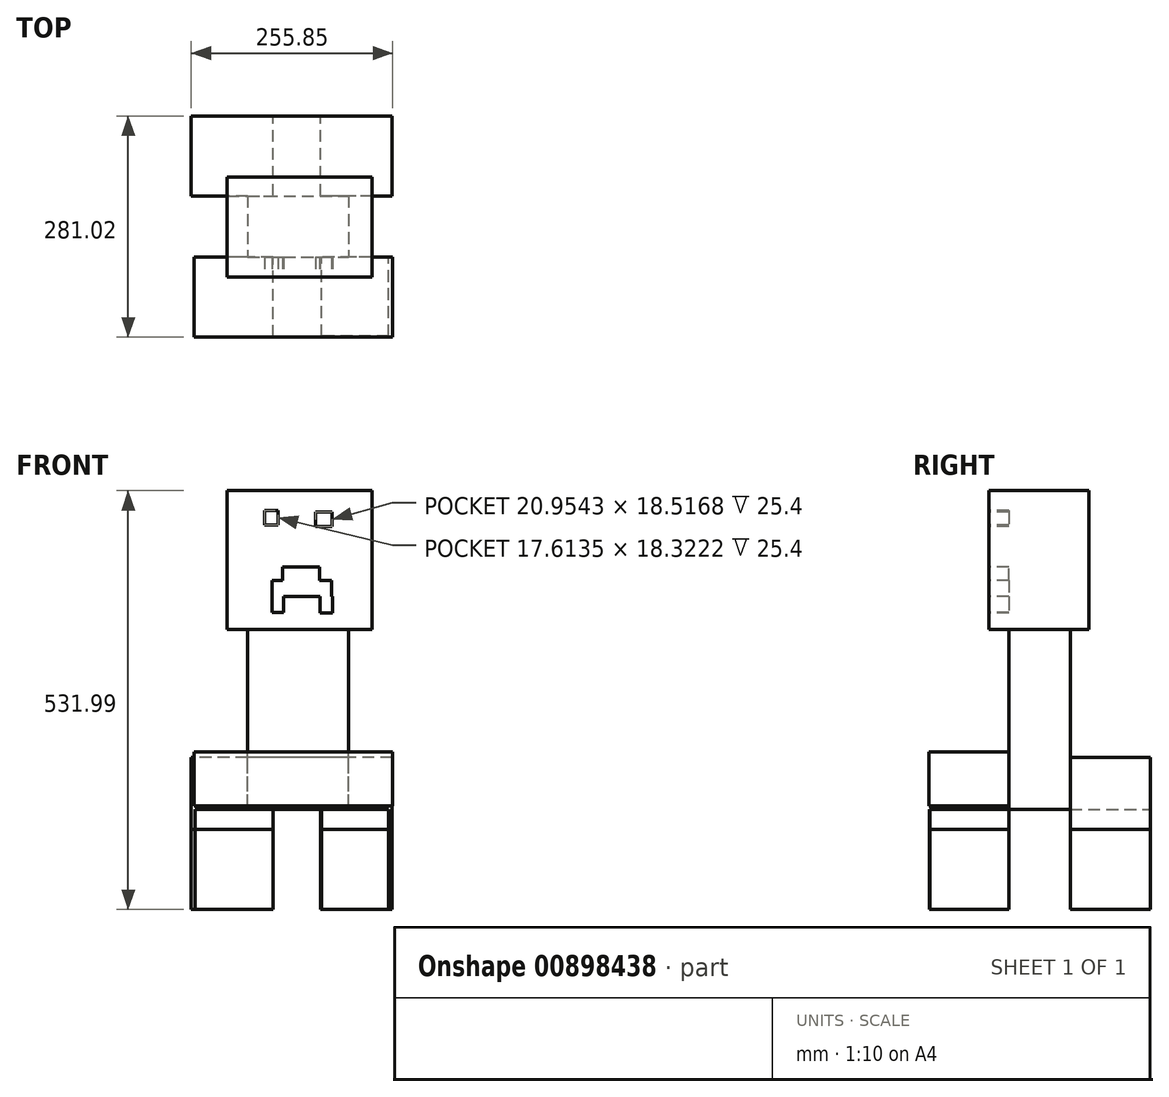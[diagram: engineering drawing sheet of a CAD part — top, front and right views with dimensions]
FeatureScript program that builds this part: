
annotation { "Feature Type Name" : "Feature", "Feature Type Description" : "" }
export const myFeature = defineFeature(function(context is Context, id is Id, definition is map)
    precondition{}
    {
        {
            var Q0;
            Q0=qCreatedBy(makeId("Front.planeOp"),FACE);
            var sketch = newSketch(context, id + "F0", { "sketchPlane" : qUnion([Q0])});
            skLineSegment(sketch, "E0.bottom", {"start": v(0, 0) * mm, "end": v(133.56, 0) * mm});
            skLineSegment(sketch, "E0.top", {"start": v(0, 176.39) * mm, "end": v(133.56, 176.39) * mm});
            skLineSegment(sketch, "E0.left", {"start": v(0, 0) * mm, "end": v(0, 176.39) * mm});
            skLineSegment(sketch, "E0.right", {"start": v(133.56, 0) * mm, "end": v(133.56, 176.39) * mm});
            skSolve(sketch);
        }
        {
            var Q0;
            Q0 = qSketchRegion(id + "F0", true);
            extrude(context, id + "F1", {"entities" : qUnion([Q0]), "depth" : 25.4 * mm, "offsetDistance" : 25.4 * mm});
        }
        {
            var Q0;
            Q0=makeQuery(id+"F1.opExtrude","CAP_FACE",FACE,{"disambiguationData":[OSD([sQuery(id+"F0.wireOp",EDGE,"E0.bottom"),sQuery(id+"F0.wireOp",EDGE,"E0.top"),sQuery(id+"F0.wireOp",EDGE,"E0.left"),sQuery(id+"F0.wireOp",EDGE,"E0.right")])],"isStart":false});
            var sketch = newSketch(context, id + "F2", { "sketchPlane" : qUnion([Q0])});
            skLineSegment(sketch, "E1.bottom", {"start": v(22.09, 151.44) * mm, "end": v(39.7, 151.44) * mm});
            skLineSegment(sketch, "E1.top", {"start": v(22.09, 133.12) * mm, "end": v(39.7, 133.12) * mm});
            skLineSegment(sketch, "E1.left", {"start": v(22.09, 151.44) * mm, "end": v(22.09, 133.12) * mm});
            skLineSegment(sketch, "E1.right", {"start": v(39.7, 151.44) * mm, "end": v(39.7, 133.12) * mm});
            skLineSegment(sketch, "E2.bottom", {"start": v(87.33, 149.32) * mm, "end": v(108.28, 149.32) * mm});
            skLineSegment(sketch, "E2.top", {"start": v(87.33, 130.8) * mm, "end": v(108.28, 130.8) * mm});
            skLineSegment(sketch, "E2.left", {"start": v(87.33, 149.32) * mm, "end": v(87.33, 130.8) * mm});
            skLineSegment(sketch, "E2.right", {"start": v(108.28, 149.32) * mm, "end": v(108.28, 130.8) * mm});
            skLineSegment(sketch, "E3.bottom", {"start": v(31.94, 62.39) * mm, "end": v(46.28, 62.39) * mm});
            skLineSegment(sketch, "E3.top", {"start": v(31.94, 21.68) * mm, "end": v(46.28, 21.68) * mm});
            skLineSegment(sketch, "E3.left", {"start": v(31.94, 62.39) * mm, "end": v(31.94, 21.68) * mm});
            skLineSegment(sketch, "E3.right", {"start": v(46.28, 62.39) * mm, "end": v(46.28, 21.68) * mm});
            skPoint(sketch, "E4.oppositeSnap0", {"position": v(46.28, 42.03) * mm});
            skLineSegment(sketch, "E4.bottom", {"start": v(46.28, 62.39) * mm, "end": v(107.18, 62.39) * mm});
            skLineSegment(sketch, "E4.top", {"start": v(46.28, 42.03) * mm, "end": v(107.18, 42.03) * mm});
            skLineSegment(sketch, "E4.left", {"start": v(46.28, 62.39) * mm, "end": v(46.28, 42.03) * mm});
            skLineSegment(sketch, "E4.right", {"start": v(107.18, 62.39) * mm, "end": v(107.18, 42.03) * mm});
            skLineSegment(sketch, "E5.bottom", {"start": v(92.98, 42.03) * mm, "end": v(108.5, 42.03) * mm});
            skLineSegment(sketch, "E5.top", {"start": v(92.98, 20.88) * mm, "end": v(108.5, 20.88) * mm});
            skLineSegment(sketch, "E5.left", {"start": v(92.98, 42.03) * mm, "end": v(92.98, 20.88) * mm});
            skLineSegment(sketch, "E5.right", {"start": v(108.5, 42.03) * mm, "end": v(108.5, 20.88) * mm});
            skSolve(sketch);
        }
        {
            var Q0;
            Q0 = qSketchRegion(id + "F2", true);
            extrude(context, id + "F3", {"entities" : qUnion([Q0]), "operationType" : NewBodyOperationType.REMOVE, "oppositeDirection" : true, "depth" : 25.4 * mm, "offsetDistance" : 25.4 * mm});
        }
        {
            var Q0;
            Q0=makeQuery(id+"F1.opExtrude","CAP_FACE",FACE,{"disambiguationData":[OSD([sQuery(id+"F0.wireOp",EDGE,"E0.bottom"),sQuery(id+"F0.wireOp",EDGE,"E0.top"),sQuery(id+"F0.wireOp",EDGE,"E0.left"),sQuery(id+"F0.wireOp",EDGE,"E0.right")])],"isStart":false});
            var sketch = newSketch(context, id + "F4", { "sketchPlane" : qUnion([Q0])});
            skLineSegment(sketch, "E6.bottom", {"start": v(45.42, 62.39) * mm, "end": v(91.85, 62.39) * mm});
            skLineSegment(sketch, "E6.top", {"start": v(45.42, 79.52) * mm, "end": v(91.85, 79.52) * mm});
            skLineSegment(sketch, "E6.left", {"start": v(45.42, 62.39) * mm, "end": v(45.42, 79.52) * mm});
            skLineSegment(sketch, "E6.right", {"start": v(91.85, 62.39) * mm, "end": v(91.85, 79.52) * mm});
            skSolve(sketch);
        }
        {
            var Q0;
            Q0 = qSketchRegion(id + "F4", true);
            extrude(context, id + "F5", {"entities" : qUnion([Q0]), "operationType" : NewBodyOperationType.REMOVE, "oppositeDirection" : true, "depth" : 25.4 * mm, "offsetDistance" : 25.4 * mm});
        }
        {
            var Q0;
            Q0=makeQuery(id+"F1.opExtrude","CAP_FACE",FACE,{"disambiguationData":[OSD([sQuery(id+"F0.wireOp",EDGE,"E0.bottom"),sQuery(id+"F0.wireOp",EDGE,"E0.top"),sQuery(id+"F0.wireOp",EDGE,"E0.left"),sQuery(id+"F0.wireOp",EDGE,"E0.right")])],"isStart":true});
            var sketch = newSketch(context, id + "F6", { "sketchPlane" : qUnion([Q0])});
            skLineSegment(sketch, "E7.bottom", {"start": v(0, 176.39) * mm, "end": v(-133.56, 176.39) * mm});
            skLineSegment(sketch, "E7.top", {"start": v(0, 0) * mm, "end": v(-133.56, 0) * mm});
            skLineSegment(sketch, "E7.left", {"start": v(0, 176.39) * mm, "end": v(0, 0) * mm});
            skLineSegment(sketch, "E7.right", {"start": v(-133.56, 176.39) * mm, "end": v(-133.56, 0) * mm});
            skSolve(sketch);
        }
        {
            var Q0;
            Q0 = qSketchRegion(id + "F6", true);
            extrude(context, id + "F7", {"entities" : qUnion([Q0]), "operationType" : NewBodyOperationType.ADD, "depth" : 101.6 * mm, "offsetDistance" : 25.4 * mm});
        }
        {
            var Q0;
            Q0=makeQuery(id+"F7.boolean.opBoolean","MERGE",FACE,{"derivedFrom":[makeQuery(id+"F1.opExtrude","SWEPT_FACE",FACE,{"disambiguationData":[OSD([sQuery(id+"F0.wireOp",EDGE,"E0.bottom")])]}),makeQuery(id+"F7.opExtrude","SWEPT_FACE",FACE,{"disambiguationData":[OSD([sQuery(id+"F6.wireOp",EDGE,"E7.top")])]})]});
            var sketch = newSketch(context, id + "F8", { "sketchPlane" : qUnion([Q0])});
            skLineSegment(sketch, "E8.bottom", {"start": v(26.18, -77.82) * mm, "end": v(103.76, -77.82) * mm});
            skLineSegment(sketch, "E8.top", {"start": v(26.18, 0) * mm, "end": v(103.76, 0) * mm});
            skLineSegment(sketch, "E8.left", {"start": v(26.18, -77.82) * mm, "end": v(26.18, 0) * mm});
            skLineSegment(sketch, "E8.right", {"start": v(103.76, -77.82) * mm, "end": v(103.76, 0) * mm});
            skSolve(sketch);
        }
        {
            var Q0;
            Q0 = qSketchRegion(id + "F8", true);
            extrude(context, id + "F9", {"entities" : qUnion([Q0]), "operationType" : NewBodyOperationType.ADD, "depth" : 25.4 * mm, "offsetDistance" : 25.4 * mm});
        }
        {
            var Q0;
            Q0=makeQuery(id+"F9.opExtrude","CAP_FACE",FACE,{"disambiguationData":[OSD([sQuery(id+"F8.wireOp",EDGE,"E8.bottom"),sQuery(id+"F8.wireOp",EDGE,"E8.top"),sQuery(id+"F8.wireOp",EDGE,"E8.left"),sQuery(id+"F8.wireOp",EDGE,"E8.right")])],"isStart":false});
            extrude(context, id + "F10", {"entities" : qUnion([Q0]), "operationType" : NewBodyOperationType.ADD, "depth" : 203.2 * mm, "offsetDistance" : 25.4 * mm});
        }
        {
            var Q0;
            Q0=makeQuery(id+"F7.boolean.opBoolean","MERGE",FACE,{"derivedFrom":[makeQuery(id+"F1.opExtrude","SWEPT_FACE",FACE,{"disambiguationData":[OSD([sQuery(id+"F0.wireOp",EDGE,"E0.right")])]}),makeQuery(id+"F7.opExtrude","SWEPT_FACE",FACE,{"disambiguationData":[OSD([sQuery(id+"F6.wireOp",EDGE,"E7.right")])]})]});
            var sketch = newSketch(context, id + "F11", { "sketchPlane" : qUnion([Q0])});
            skLineSegment(sketch, "E9.bottom", {"start": v(-25.4, 176.39) * mm, "end": v(101.6, 176.39) * mm});
            skLineSegment(sketch, "E9.top", {"start": v(-25.4, 0) * mm, "end": v(101.6, 0) * mm});
            skLineSegment(sketch, "E9.left", {"start": v(-25.4, 176.39) * mm, "end": v(-25.4, 0) * mm});
            skLineSegment(sketch, "E9.right", {"start": v(101.6, 176.39) * mm, "end": v(101.6, 0) * mm});
            skSolve(sketch);
        }
        {
            var Q0;
            Q0 = qSketchRegion(id + "F11", true);
            extrude(context, id + "F12", {"entities" : qUnion([Q0]), "operationType" : NewBodyOperationType.ADD, "depth" : 25.4 * mm, "offsetDistance" : 25.4 * mm});
        }
        {
            var Q0;
            Q0=makeQuery(id+"F7.boolean.opBoolean","MERGE",FACE,{"derivedFrom":[makeQuery(id+"F1.opExtrude","SWEPT_FACE",FACE,{"disambiguationData":[OSD([sQuery(id+"F0.wireOp",EDGE,"E0.left")])]}),makeQuery(id+"F7.opExtrude","SWEPT_FACE",FACE,{"disambiguationData":[OSD([sQuery(id+"F6.wireOp",EDGE,"E7.left")])]})]});
            var sketch = newSketch(context, id + "F13", { "sketchPlane" : qUnion([Q0])});
            skLineSegment(sketch, "E10.bottom", {"start": v(-101.6, 176.39) * mm, "end": v(25.4, 176.39) * mm});
            skLineSegment(sketch, "E10.top", {"start": v(-101.6, 0) * mm, "end": v(25.4, 0) * mm});
            skLineSegment(sketch, "E10.left", {"start": v(-101.6, 176.39) * mm, "end": v(-101.6, 0) * mm});
            skLineSegment(sketch, "E10.right", {"start": v(25.4, 176.39) * mm, "end": v(25.4, 0) * mm});
            skSolve(sketch);
        }
        {
            var Q0;
            Q0 = qSketchRegion(id + "F13", true);
            extrude(context, id + "F14", {"entities" : qUnion([Q0]), "operationType" : NewBodyOperationType.ADD, "depth" : 25.4 * mm, "offsetDistance" : 25.4 * mm});
        }
        {
            var Q0;
            {var subQ0=sQuery(id+"F8.wireOp",EDGE,"E8.right");Q0=makeQuery(id+"F10.boolean.opBoolean","MERGE",FACE,{"derivedFrom":[makeQuery(id+"F9.opExtrude","SWEPT_FACE",FACE,{"disambiguationData":[OSD([subQ0])]}),makeQuery(id+"F10.opExtrude","SWEPT_FACE",FACE,{"disambiguationData":[OSD([subQ0])]})]});}
            var sketch = newSketch(context, id + "F15", { "sketchPlane" : qUnion([Q0])});
            skLineSegment(sketch, "E11.bottom", {"start": v(77.82, 0) * mm, "end": v(0, 0) * mm});
            skLineSegment(sketch, "E11.top", {"start": v(77.82, -228.6) * mm, "end": v(0, -228.6) * mm});
            skLineSegment(sketch, "E11.left", {"start": v(77.82, 0) * mm, "end": v(77.82, -228.6) * mm});
            skLineSegment(sketch, "E11.right", {"start": v(0, 0) * mm, "end": v(0, -228.6) * mm});
            skSolve(sketch);
        }
        {
            var Q0;
            Q0 = qSketchRegion(id + "F15", true);
            extrude(context, id + "F16", {"entities" : qUnion([Q0]), "operationType" : NewBodyOperationType.ADD, "depth" : 25.4 * mm, "offsetDistance" : 25.4 * mm});
        }
        {
            var Q0;
            {var subQ0=sQuery(id+"F8.wireOp",EDGE,"E8.left");Q0=makeQuery(id+"F10.boolean.opBoolean","MERGE",FACE,{"derivedFrom":[makeQuery(id+"F9.opExtrude","SWEPT_FACE",FACE,{"disambiguationData":[OSD([subQ0])]}),makeQuery(id+"F10.opExtrude","SWEPT_FACE",FACE,{"disambiguationData":[OSD([subQ0])]})]});}
            var sketch = newSketch(context, id + "F17", { "sketchPlane" : qUnion([Q0])});
            skLineSegment(sketch, "E12.bottom", {"start": v(-77.82, 0) * mm, "end": v(0, 0) * mm});
            skLineSegment(sketch, "E12.top", {"start": v(-77.82, -228.6) * mm, "end": v(0, -228.6) * mm});
            skLineSegment(sketch, "E12.left", {"start": v(-77.82, 0) * mm, "end": v(-77.82, -228.6) * mm});
            skLineSegment(sketch, "E12.right", {"start": v(0, 0) * mm, "end": v(0, -228.6) * mm});
            skSolve(sketch);
        }
        {
            var Q0;
            Q0 = qSketchRegion(id + "F17", true);
            extrude(context, id + "F18", {"entities" : qUnion([Q0]), "operationType" : NewBodyOperationType.ADD, "depth" : 25.4 * mm, "offsetDistance" : 25.4 * mm});
        }
        {
            var Q0;
            {var subQ0=sQuery(id+"F8.wireOp",EDGE,"E8.bottom");Q0=makeQuery(id+"F18.boolean.opBoolean","MERGE",FACE,{"derivedFrom":[makeQuery(id+"F16.boolean.opBoolean","MERGE",FACE,{"derivedFrom":[makeQuery(id+"F10.boolean.opBoolean","MERGE",FACE,{"derivedFrom":[makeQuery(id+"F9.opExtrude","SWEPT_FACE",FACE,{"disambiguationData":[OSD([subQ0])]}),makeQuery(id+"F10.opExtrude","SWEPT_FACE",FACE,{"disambiguationData":[OSD([subQ0])]})]}),makeQuery(id+"F16.opExtrude","SWEPT_FACE",FACE,{"disambiguationData":[OSD([sQuery(id+"F15.wireOp",EDGE,"E11.left")])]})]}),makeQuery(id+"F18.opExtrude","SWEPT_FACE",FACE,{"disambiguationData":[OSD([sQuery(id+"F17.wireOp",EDGE,"E12.left")])]})]});}
            var sketch = newSketch(context, id + "F19", { "sketchPlane" : qUnion([Q0])});
            skLineSegment(sketch, "E13.bottom", {"start": v(-184.48, -162.14) * mm, "end": v(70.84, -162.14) * mm});
            skLineSegment(sketch, "E13.top", {"start": v(-184.48, -228.6) * mm, "end": v(70.84, -228.6) * mm});
            skLineSegment(sketch, "E13.left", {"start": v(-184.48, -162.14) * mm, "end": v(-184.48, -228.6) * mm});
            skLineSegment(sketch, "E13.right", {"start": v(70.84, -162.14) * mm, "end": v(70.84, -228.6) * mm});
            skSolve(sketch);
        }
        {
            var Q0;
            Q0 = qSketchRegion(id + "F19", true);
            extrude(context, id + "F20", {"entities" : qUnion([Q0]), "operationType" : NewBodyOperationType.ADD, "depth" : 101.6 * mm, "offsetDistance" : 25.4 * mm});
        }
        {
            var Q0;
            {var subQ0=sQuery(id+"F8.wireOp",EDGE,"E8.top");Q0=makeQuery(id+"F18.boolean.opBoolean","MERGE",FACE,{"derivedFrom":[makeQuery(id+"F16.boolean.opBoolean","MERGE",FACE,{"derivedFrom":[makeQuery(id+"F10.boolean.opBoolean","MERGE",FACE,{"derivedFrom":[makeQuery(id+"F9.opExtrude","SWEPT_FACE",FACE,{"disambiguationData":[OSD([subQ0])]}),makeQuery(id+"F10.opExtrude","SWEPT_FACE",FACE,{"disambiguationData":[OSD([subQ0])]})]}),makeQuery(id+"F16.opExtrude","SWEPT_FACE",FACE,{"disambiguationData":[OSD([sQuery(id+"F15.wireOp",EDGE,"E11.right")])]})]}),makeQuery(id+"F18.opExtrude","SWEPT_FACE",FACE,{"disambiguationData":[OSD([sQuery(id+"F17.wireOp",EDGE,"E12.right")])]})]});}
            var sketch = newSketch(context, id + "F21", { "sketchPlane" : qUnion([Q0])});
            skLineSegment(sketch, "E14.bottom", {"start": v(185, -155.25) * mm, "end": v(-67.14, -155.25) * mm});
            skLineSegment(sketch, "E14.top", {"start": v(185, -224.22) * mm, "end": v(-67.14, -224.22) * mm});
            skLineSegment(sketch, "E14.left", {"start": v(185, -155.25) * mm, "end": v(185, -224.22) * mm});
            skLineSegment(sketch, "E14.right", {"start": v(-67.14, -155.25) * mm, "end": v(-67.14, -224.22) * mm});
            skSolve(sketch);
        }
        {
            var Q0;
            Q0 = qSketchRegion(id + "F21", true);
            extrude(context, id + "F22", {"entities" : qUnion([Q0]), "operationType" : NewBodyOperationType.ADD, "depth" : 101.6 * mm, "offsetDistance" : 25.4 * mm});
        }
        {
            var Q0;
            Q0=makeQuery(id+"F20.boolean.opBoolean","MERGE",FACE,{"derivedFrom":[makeQuery(id+"F18.boolean.opBoolean","MERGE",FACE,{"derivedFrom":[makeQuery(id+"F16.boolean.opBoolean","MERGE",FACE,{"derivedFrom":[makeQuery(id+"F10.opExtrude","CAP_FACE",FACE,{"disambiguationData":[OSD([sQuery(id+"F8.wireOp",EDGE,"E8.bottom"),sQuery(id+"F8.wireOp",EDGE,"E8.top"),sQuery(id+"F8.wireOp",EDGE,"E8.left"),sQuery(id+"F8.wireOp",EDGE,"E8.right")])],"isStart":false}),makeQuery(id+"F16.opExtrude","SWEPT_FACE",FACE,{"disambiguationData":[OSD([sQuery(id+"F15.wireOp",EDGE,"E11.top")])]})]}),makeQuery(id+"F18.opExtrude","SWEPT_FACE",FACE,{"disambiguationData":[OSD([sQuery(id+"F17.wireOp",EDGE,"E12.top")])]})]}),makeQuery(id+"F20.opExtrude","SWEPT_FACE",FACE,{"disambiguationData":[OSD([sQuery(id+"F19.wireOp",EDGE,"E13.top")])]})]});
            var sketch = newSketch(context, id + "F23", { "sketchPlane" : qUnion([Q0])});
            skLineSegment(sketch, "E15.bottom", {"start": v(180, 100.27) * mm, "end": v(94.37, 100.27) * mm});
            skLineSegment(sketch, "E15.top", {"start": v(180, 0) * mm, "end": v(94.37, 0) * mm});
            skLineSegment(sketch, "E15.left", {"start": v(180, 100.27) * mm, "end": v(180, 0) * mm});
            skLineSegment(sketch, "E15.right", {"start": v(94.37, 100.27) * mm, "end": v(94.37, 0) * mm});
            skLineSegment(sketch, "E16.bottom", {"start": v(33.06, 101.2) * mm, "end": v(-66.15, 101.2) * mm});
            skLineSegment(sketch, "E16.top", {"start": v(33.06, 0) * mm, "end": v(-66.15, 0) * mm});
            skLineSegment(sketch, "E16.left", {"start": v(33.06, 101.2) * mm, "end": v(33.06, 0) * mm});
            skLineSegment(sketch, "E16.right", {"start": v(-66.15, 101.2) * mm, "end": v(-66.15, 0) * mm});
            skLineSegment(sketch, "E17.bottom", {"start": v(-70.84, -77.82) * mm, "end": v(33.06, -77.82) * mm});
            skLineSegment(sketch, "E17.top", {"start": v(-70.84, -179.42) * mm, "end": v(33.06, -179.42) * mm});
            skLineSegment(sketch, "E17.left", {"start": v(-70.84, -77.82) * mm, "end": v(-70.84, -179.42) * mm});
            skLineSegment(sketch, "E17.right", {"start": v(33.06, -77.82) * mm, "end": v(33.06, -179.42) * mm});
            skLineSegment(sketch, "E18.bottom", {"start": v(184.48, -77.82) * mm, "end": v(93.34, -77.82) * mm});
            skLineSegment(sketch, "E18.top", {"start": v(184.48, -179.42) * mm, "end": v(93.34, -179.42) * mm});
            skLineSegment(sketch, "E18.left", {"start": v(184.48, -77.82) * mm, "end": v(184.48, -179.42) * mm});
            skLineSegment(sketch, "E18.right", {"start": v(93.34, -77.82) * mm, "end": v(93.34, -179.42) * mm});
            skSolve(sketch);
        }
        {
            var Q0;
            Q0=makeQuery(id+"F23.imprint","IMPRINT",FACE,{"disambiguationData":[TD([[makeQuery(id+"F23.imprint","IMPRINT",EDGE,{"derivedFrom":sQuery(id+"F23.wireOp",EDGE,"E18.top")}),-1.0]])]});
            var Q1;
            Q1=makeQuery(id+"F23.imprint","IMPRINT",FACE,{"disambiguationData":[TD([[makeQuery(id+"F23.imprint","IMPRINT",EDGE,{"derivedFrom":sQuery(id+"F23.wireOp",EDGE,"E17.top")}),-1.0]])]});
            var Q2;
            Q2=makeQuery(id+"F23.imprint","IMPRINT",FACE,{"disambiguationData":[TD([[makeQuery(id+"F23.imprint","IMPRINT",EDGE,{"derivedFrom":sQuery(id+"F23.wireOp",EDGE,"E16.bottom")}),1.0]])]});
            var Q3;
            Q3=makeQuery(id+"F23.imprint","IMPRINT",FACE,{"disambiguationData":[TD([[makeQuery(id+"F23.imprint","IMPRINT",EDGE,{"derivedFrom":sQuery(id+"F23.wireOp",EDGE,"E15.bottom")}),1.0]])]});
            extrude(context, id + "F24", {"entities" : qUnion([Q0, Q1, Q2, Q3]), "operationType" : NewBodyOperationType.ADD, "depth" : 25.4 * mm, "offsetDistance" : 25.4 * mm});
        }
        {
            var Q0;
            Q0=makeQuery(id+"F24.opExtrude","CAP_FACE",FACE,{"disambiguationData":[OSD([sQuery(id+"F23.wireOp",EDGE,"E15.bottom"),sQuery(id+"F23.wireOp",EDGE,"E15.top"),sQuery(id+"F23.wireOp",EDGE,"E15.left"),sQuery(id+"F23.wireOp",EDGE,"E15.right")])],"isStart":false});
            var Q1;
            Q1=makeQuery(id+"F24.opExtrude","CAP_FACE",FACE,{"disambiguationData":[OSD([sQuery(id+"F23.wireOp",EDGE,"E16.bottom"),sQuery(id+"F23.wireOp",EDGE,"E16.top"),sQuery(id+"F23.wireOp",EDGE,"E16.left"),sQuery(id+"F23.wireOp",EDGE,"E16.right")])],"isStart":false});
            var Q2;
            Q2=makeQuery(id+"F24.opExtrude","CAP_FACE",FACE,{"disambiguationData":[OSD([sQuery(id+"F23.wireOp",EDGE,"E17.bottom"),sQuery(id+"F23.wireOp",EDGE,"E17.top"),sQuery(id+"F23.wireOp",EDGE,"E17.left"),sQuery(id+"F23.wireOp",EDGE,"E17.right")])],"isStart":false});
            var Q3;
            Q3=makeQuery(id+"F24.opExtrude","CAP_FACE",FACE,{"disambiguationData":[OSD([sQuery(id+"F23.wireOp",EDGE,"E18.bottom"),sQuery(id+"F23.wireOp",EDGE,"E18.top"),sQuery(id+"F23.wireOp",EDGE,"E18.left"),sQuery(id+"F23.wireOp",EDGE,"E18.right")])],"isStart":false});
            extrude(context, id + "F25", {"entities" : qUnion([Q0, Q1, Q2, Q3]), "depth" : 101.6 * mm, "offsetDistance" : 25.4 * mm});
        }
    });
